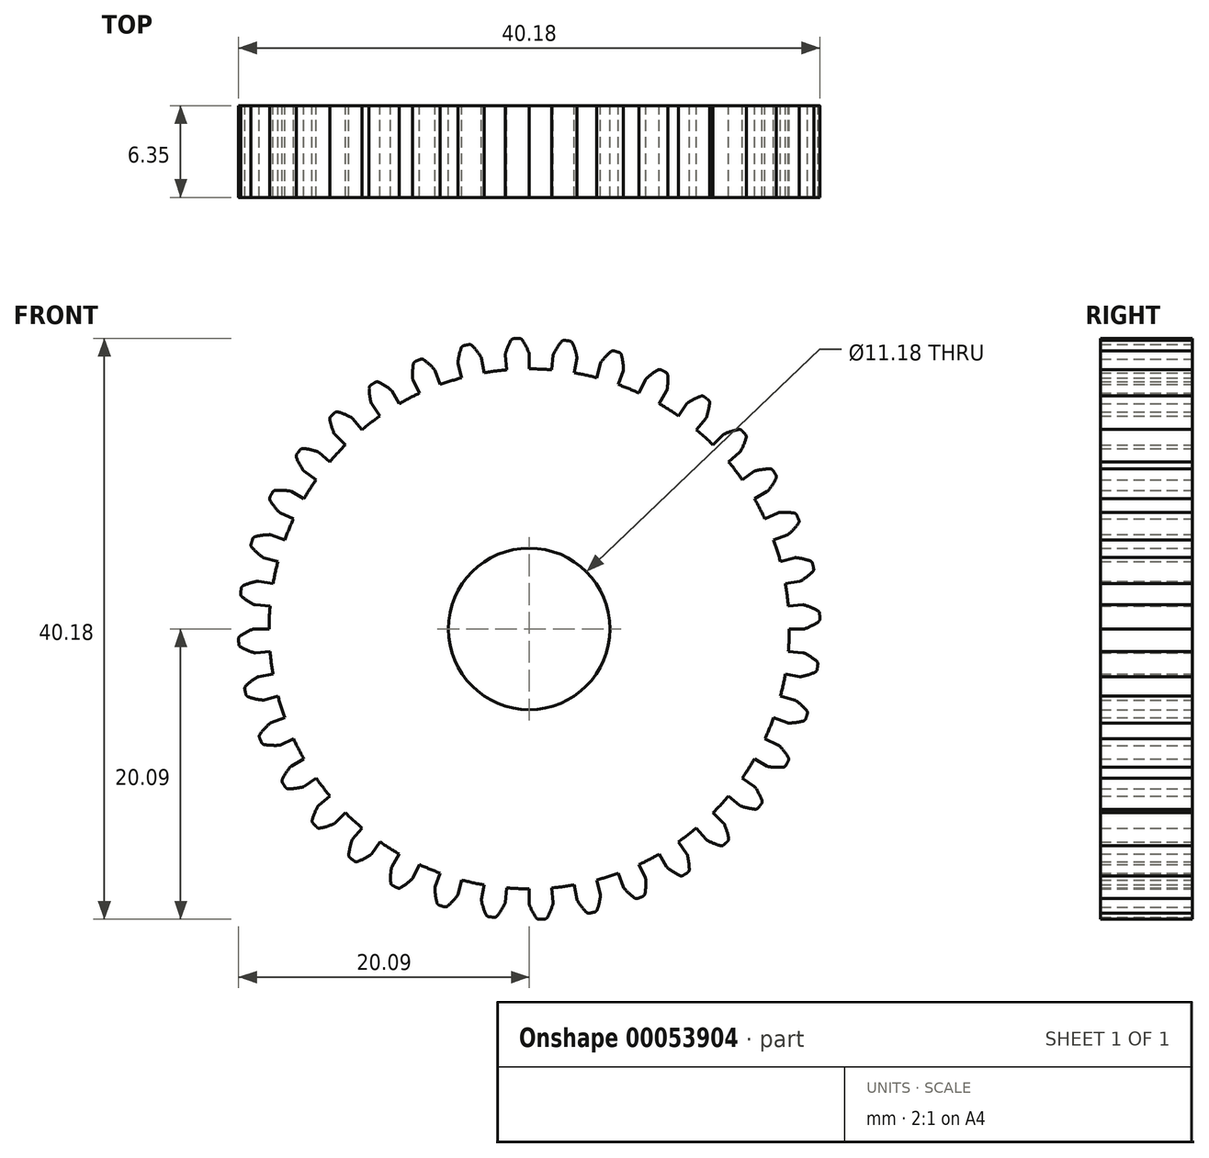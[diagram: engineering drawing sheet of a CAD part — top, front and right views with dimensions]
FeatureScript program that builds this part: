
annotation { "Feature Type Name" : "Feature", "Feature Type Description" : "" }
export const myFeature = defineFeature(function(context is Context, id is Id, definition is map)
    precondition{}
    {
        {
            var Q0;
            Q0=qCreatedBy(makeId("Front.planeOp"),FACE);
            var sketch = newSketch(context, id + "F0", { "sketchPlane" : qUnion([Q0])});
            skCircle(sketch, "E0", {"center": v(0, 0) * mm, "radius": 17.98 * mm});
            skArc(sketch, "E1", {"start": v(-0.7, 20.1) * mm, "mid": v(-0.79, 20.09) * mm, "end": v(-0.88, 20.08) * mm});
            skArc(sketch, "E2.trimOffspring", {"start": v(-0.02, 19.1) * mm, "mid": v(-0.23, 19.55) * mm, "end": v(-0.48, 19.98) * mm});
            skLineSegment(sketch, "E3", {"start": v(0, 19) * mm, "end": v(0, 17.98) * mm});
            skArc(sketch, "E4.MirrorCS", {"start": v(-1.05, 20.08) * mm, "mid": v(-0.97, 20.08) * mm, "end": v(-0.88, 20.08) * mm});
            skArc(sketch, "E5.MirrorCS", {"start": v(-1.65, 19.02) * mm, "mid": v(-1.48, 19.5) * mm, "end": v(-1.26, 19.94) * mm});
            skLineSegment(sketch, "E6.MirrorCS", {"start": v(-1.66, 18.93) * mm, "end": v(-1.57, 17.91) * mm});
            skPoint(sketch, "E7.visualSharp", {"position": v(-1.66, 18.98) * mm});
            skArc(sketch, "E7.filletArc", {"start": v(-1.65, 19.02) * mm, "mid": v(-1.66, 18.98) * mm, "end": v(-1.66, 18.93) * mm});
            skPoint(sketch, "E8.visualSharp", {"position": v(-1.2, 20.07) * mm});
            skArc(sketch, "E8.filletArc", {"start": v(-1.05, 20.08) * mm, "mid": v(-1.18, 20.04) * mm, "end": v(-1.26, 19.94) * mm});
            skPoint(sketch, "E9.visualSharp", {"position": v(-0.56, 20.1) * mm});
            skArc(sketch, "E9.filletArc", {"start": v(-0.48, 19.98) * mm, "mid": v(-0.58, 20.06) * mm, "end": v(-0.7, 20.1) * mm});
            skPoint(sketch, "E10.visualSharp", {"position": v(0, 19.05) * mm});
            skArc(sketch, "E10.filletArc", {"start": v(0, 19) * mm, "mid": v(0, 19.05) * mm, "end": v(-0.02, 19.1) * mm});
            skLineSegment(sketch, "E11.1.0", {"start": v(-3.3, 18.71) * mm, "end": v(-3.12, 17.7) * mm});
            skPoint(sketch, "E11.1.1", {"position": v(-4.93, 18.4) * mm});
            skArc(sketch, "E11.1.2", {"start": v(-3.33, 18.8) * mm, "mid": v(-3.62, 19.21) * mm, "end": v(-3.94, 19.6) * mm});
            skPoint(sketch, "E11.1.3", {"position": v(-3.3, 18.76) * mm});
            skArc(sketch, "E11.1.4", {"start": v(-4.93, 18.45) * mm, "mid": v(-4.84, 18.94) * mm, "end": v(-4.7, 19.42) * mm});
            skPoint(sketch, "E11.1.5", {"position": v(-4.66, 19.56) * mm});
            skPoint(sketch, "E11.1.6", {"position": v(-4.04, 19.7) * mm});
            skLineSegment(sketch, "E11.1.7", {"start": v(-4.92, 18.35) * mm, "end": v(-4.65, 17.37) * mm});
            skArc(sketch, "E11.1.8", {"start": v(-4.52, 19.59) * mm, "mid": v(-4.64, 19.53) * mm, "end": v(-4.7, 19.42) * mm});
            skArc(sketch, "E11.1.9", {"start": v(-4.52, 19.59) * mm, "mid": v(-4.44, 19.6) * mm, "end": v(-4.35, 19.63) * mm});
            skArc(sketch, "E11.1.10", {"start": v(-3.94, 19.6) * mm, "mid": v(-4.05, 19.66) * mm, "end": v(-4.18, 19.67) * mm});
            skArc(sketch, "E11.1.11", {"start": v(-4.18, 19.67) * mm, "mid": v(-4.27, 19.65) * mm, "end": v(-4.35, 19.63) * mm});
            skArc(sketch, "E11.1.12", {"start": v(-4.93, 18.45) * mm, "mid": v(-4.93, 18.4) * mm, "end": v(-4.92, 18.35) * mm});
            skArc(sketch, "E11.1.13", {"start": v(-3.3, 18.71) * mm, "mid": v(-3.31, 18.76) * mm, "end": v(-3.33, 18.8) * mm});
            skLineSegment(sketch, "E11.2.0", {"start": v(-6.5, 17.86) * mm, "end": v(-6.15, 16.9) * mm});
            skPoint(sketch, "E11.2.1", {"position": v(-8.05, 17.27) * mm});
            skArc(sketch, "E11.2.2", {"start": v(-6.55, 17.94) * mm, "mid": v(-6.9, 18.3) * mm, "end": v(-7.28, 18.6) * mm});
            skPoint(sketch, "E11.2.3", {"position": v(-6.52, 17.9) * mm});
            skArc(sketch, "E11.2.4", {"start": v(-8.05, 17.31) * mm, "mid": v(-8.06, 17.81) * mm, "end": v(-8, 18.3) * mm});
            skPoint(sketch, "E11.2.5", {"position": v(-7.98, 18.45) * mm});
            skPoint(sketch, "E11.2.6", {"position": v(-7.4, 18.7) * mm});
            skLineSegment(sketch, "E11.2.7", {"start": v(-8.03, 17.22) * mm, "end": v(-7.6, 16.3) * mm});
            skArc(sketch, "E11.2.8", {"start": v(-7.86, 18.5) * mm, "mid": v(-7.96, 18.43) * mm, "end": v(-8, 18.3) * mm});
            skArc(sketch, "E11.2.9", {"start": v(-7.86, 18.5) * mm, "mid": v(-7.78, 18.54) * mm, "end": v(-7.7, 18.57) * mm});
            skArc(sketch, "E11.2.10", {"start": v(-7.28, 18.6) * mm, "mid": v(-7.4, 18.66) * mm, "end": v(-7.53, 18.64) * mm});
            skArc(sketch, "E11.2.11", {"start": v(-7.53, 18.64) * mm, "mid": v(-7.61, 18.6) * mm, "end": v(-7.7, 18.57) * mm});
            skArc(sketch, "E11.2.12", {"start": v(-8.05, 17.31) * mm, "mid": v(-8.05, 17.27) * mm, "end": v(-8.03, 17.22) * mm});
            skArc(sketch, "E11.2.13", {"start": v(-6.5, 17.86) * mm, "mid": v(-6.52, 17.9) * mm, "end": v(-6.55, 17.94) * mm});
            skLineSegment(sketch, "E11.3.0", {"start": v(-9.5, 16.46) * mm, "end": v(-9, 15.57) * mm});
            skPoint(sketch, "E11.3.1", {"position": v(-10.93, 15.6) * mm});
            skArc(sketch, "E11.3.2", {"start": v(-9.56, 16.53) * mm, "mid": v(-9.97, 16.82) * mm, "end": v(-10.4, 17.06) * mm});
            skPoint(sketch, "E11.3.3", {"position": v(-9.52, 16.5) * mm});
            skArc(sketch, "E11.3.4", {"start": v(-10.94, 15.65) * mm, "mid": v(-11.03, 16.14) * mm, "end": v(-11.07, 16.64) * mm});
            skPoint(sketch, "E11.3.5", {"position": v(-11.07, 16.78) * mm});
            skPoint(sketch, "E11.3.6", {"position": v(-10.53, 17.12) * mm});
            skLineSegment(sketch, "E11.3.7", {"start": v(-10.9, 15.57) * mm, "end": v(-10.31, 14.73) * mm});
            skArc(sketch, "E11.3.8", {"start": v(-10.95, 16.86) * mm, "mid": v(-11.04, 16.77) * mm, "end": v(-11.07, 16.64) * mm});
            skArc(sketch, "E11.3.9", {"start": v(-10.95, 16.86) * mm, "mid": v(-10.88, 16.9) * mm, "end": v(-10.8, 16.96) * mm});
            skArc(sketch, "E11.3.10", {"start": v(-10.4, 17.06) * mm, "mid": v(-10.53, 17.09) * mm, "end": v(-10.65, 17.05) * mm});
            skArc(sketch, "E11.3.11", {"start": v(-10.65, 17.05) * mm, "mid": v(-10.73, 17) * mm, "end": v(-10.8, 16.96) * mm});
            skArc(sketch, "E11.3.12", {"start": v(-10.94, 15.65) * mm, "mid": v(-10.92, 15.6) * mm, "end": v(-10.9, 15.57) * mm});
            skArc(sketch, "E11.3.13", {"start": v(-9.5, 16.46) * mm, "mid": v(-9.53, 16.5) * mm, "end": v(-9.56, 16.53) * mm});
            skLineSegment(sketch, "E11.4.0", {"start": v(-12.21, 14.56) * mm, "end": v(-11.56, 13.78) * mm});
            skPoint(sketch, "E11.4.1", {"position": v(-13.47, 13.47) * mm});
            skArc(sketch, "E11.4.2", {"start": v(-12.29, 14.62) * mm, "mid": v(-12.74, 14.83) * mm, "end": v(-13.2, 15) * mm});
            skPoint(sketch, "E11.4.3", {"position": v(-12.25, 14.6) * mm});
            skArc(sketch, "E11.4.4", {"start": v(-13.5, 13.52) * mm, "mid": v(-13.66, 13.98) * mm, "end": v(-13.79, 14.47) * mm});
            skPoint(sketch, "E11.4.5", {"position": v(-13.81, 14.6) * mm});
            skPoint(sketch, "E11.4.6", {"position": v(-13.35, 15.03) * mm});
            skLineSegment(sketch, "E11.4.7", {"start": v(-13.44, 13.44) * mm, "end": v(-12.72, 12.72) * mm});
            skArc(sketch, "E11.4.8", {"start": v(-13.71, 14.7) * mm, "mid": v(-13.78, 14.6) * mm, "end": v(-13.79, 14.47) * mm});
            skArc(sketch, "E11.4.9", {"start": v(-13.71, 14.7) * mm, "mid": v(-13.65, 14.76) * mm, "end": v(-13.58, 14.82) * mm});
            skArc(sketch, "E11.4.10", {"start": v(-13.2, 15) * mm, "mid": v(-13.34, 15) * mm, "end": v(-13.45, 14.94) * mm});
            skArc(sketch, "E11.4.11", {"start": v(-13.45, 14.94) * mm, "mid": v(-13.52, 14.88) * mm, "end": v(-13.58, 14.82) * mm});
            skArc(sketch, "E11.4.12", {"start": v(-13.5, 13.52) * mm, "mid": v(-13.47, 13.47) * mm, "end": v(-13.44, 13.44) * mm});
            skArc(sketch, "E11.4.13", {"start": v(-12.21, 14.56) * mm, "mid": v(-12.25, 14.6) * mm, "end": v(-12.29, 14.62) * mm});
            skLineSegment(sketch, "E11.5.0", {"start": v(-14.56, 12.21) * mm, "end": v(-13.78, 11.56) * mm});
            skPoint(sketch, "E11.5.1", {"position": v(-15.6, 10.93) * mm});
            skArc(sketch, "E11.5.2", {"start": v(-14.64, 12.26) * mm, "mid": v(-15.12, 12.4) * mm, "end": v(-15.61, 12.47) * mm});
            skPoint(sketch, "E11.5.3", {"position": v(-14.6, 12.25) * mm});
            skArc(sketch, "E11.5.4", {"start": v(-15.63, 10.97) * mm, "mid": v(-15.88, 11.4) * mm, "end": v(-16.1, 11.85) * mm});
            skPoint(sketch, "E11.5.5", {"position": v(-16.14, 11.99) * mm});
            skPoint(sketch, "E11.5.6", {"position": v(-15.76, 12.49) * mm});
            skLineSegment(sketch, "E11.5.7", {"start": v(-15.57, 10.9) * mm, "end": v(-14.73, 10.31) * mm});
            skArc(sketch, "E11.5.8", {"start": v(-16.06, 12.1) * mm, "mid": v(-16.1, 11.98) * mm, "end": v(-16.1, 11.85) * mm});
            skArc(sketch, "E11.5.9", {"start": v(-16.06, 12.1) * mm, "mid": v(-16, 12.17) * mm, "end": v(-15.95, 12.24) * mm});
            skArc(sketch, "E11.5.10", {"start": v(-15.61, 12.47) * mm, "mid": v(-15.74, 12.46) * mm, "end": v(-15.84, 12.38) * mm});
            skArc(sketch, "E11.5.11", {"start": v(-15.84, 12.38) * mm, "mid": v(-15.9, 12.3) * mm, "end": v(-15.95, 12.24) * mm});
            skArc(sketch, "E11.5.12", {"start": v(-15.63, 10.97) * mm, "mid": v(-15.6, 10.93) * mm, "end": v(-15.57, 10.9) * mm});
            skArc(sketch, "E11.5.13", {"start": v(-14.56, 12.21) * mm, "mid": v(-14.6, 12.24) * mm, "end": v(-14.64, 12.26) * mm});
            skLineSegment(sketch, "E11.6.0", {"start": v(-16.46, 9.5) * mm, "end": v(-15.57, 9) * mm});
            skPoint(sketch, "E11.6.1", {"position": v(-17.27, 8.05) * mm});
            skArc(sketch, "E11.6.2", {"start": v(-16.55, 9.53) * mm, "mid": v(-17.04, 9.58) * mm, "end": v(-17.54, 9.57) * mm});
            skPoint(sketch, "E11.6.3", {"position": v(-16.5, 9.53) * mm});
            skArc(sketch, "E11.6.4", {"start": v(-17.3, 8.09) * mm, "mid": v(-17.62, 8.47) * mm, "end": v(-17.9, 8.88) * mm});
            skPoint(sketch, "E11.6.5", {"position": v(-17.98, 9) * mm});
            skPoint(sketch, "E11.6.6", {"position": v(-17.68, 9.56) * mm});
            skLineSegment(sketch, "E11.6.7", {"start": v(-17.22, 8.03) * mm, "end": v(-16.3, 7.6) * mm});
            skArc(sketch, "E11.6.8", {"start": v(-17.91, 9.13) * mm, "mid": v(-17.94, 9) * mm, "end": v(-17.9, 8.88) * mm});
            skArc(sketch, "E11.6.9", {"start": v(-17.91, 9.13) * mm, "mid": v(-17.87, 9.2) * mm, "end": v(-17.83, 9.28) * mm});
            skArc(sketch, "E11.6.10", {"start": v(-17.54, 9.57) * mm, "mid": v(-17.66, 9.53) * mm, "end": v(-17.75, 9.44) * mm});
            skArc(sketch, "E11.6.11", {"start": v(-17.75, 9.44) * mm, "mid": v(-17.8, 9.36) * mm, "end": v(-17.83, 9.28) * mm});
            skArc(sketch, "E11.6.12", {"start": v(-17.3, 8.09) * mm, "mid": v(-17.26, 8.05) * mm, "end": v(-17.22, 8.03) * mm});
            skArc(sketch, "E11.6.13", {"start": v(-16.46, 9.5) * mm, "mid": v(-16.5, 9.52) * mm, "end": v(-16.55, 9.53) * mm});
            skLineSegment(sketch, "E11.7.0", {"start": v(-17.86, 6.5) * mm, "end": v(-16.9, 6.15) * mm});
            skPoint(sketch, "E11.7.1", {"position": v(-18.4, 4.93) * mm});
            skArc(sketch, "E11.7.2", {"start": v(-17.95, 6.51) * mm, "mid": v(-18.45, 6.47) * mm, "end": v(-18.94, 6.38) * mm});
            skPoint(sketch, "E11.7.3", {"position": v(-17.9, 6.52) * mm});
            skArc(sketch, "E11.7.4", {"start": v(-18.44, 4.96) * mm, "mid": v(-18.82, 5.28) * mm, "end": v(-19.17, 5.63) * mm});
            skPoint(sketch, "E11.7.5", {"position": v(-19.27, 5.74) * mm});
            skPoint(sketch, "E11.7.6", {"position": v(-19.08, 6.35) * mm});
            skLineSegment(sketch, "E11.7.7", {"start": v(-18.35, 4.92) * mm, "end": v(-17.37, 4.65) * mm});
            skArc(sketch, "E11.7.8", {"start": v(-19.23, 5.88) * mm, "mid": v(-19.23, 5.75) * mm, "end": v(-19.17, 5.63) * mm});
            skArc(sketch, "E11.7.9", {"start": v(-19.23, 5.88) * mm, "mid": v(-19.2, 5.96) * mm, "end": v(-19.17, 6.05) * mm});
            skArc(sketch, "E11.7.10", {"start": v(-18.94, 6.38) * mm, "mid": v(-19.05, 6.32) * mm, "end": v(-19.12, 6.21) * mm});
            skArc(sketch, "E11.7.11", {"start": v(-19.12, 6.21) * mm, "mid": v(-19.15, 6.13) * mm, "end": v(-19.17, 6.05) * mm});
            skArc(sketch, "E11.7.12", {"start": v(-18.44, 4.96) * mm, "mid": v(-18.4, 4.93) * mm, "end": v(-18.35, 4.92) * mm});
            skArc(sketch, "E11.7.13", {"start": v(-17.86, 6.5) * mm, "mid": v(-17.9, 6.51) * mm, "end": v(-17.95, 6.51) * mm});
            skLineSegment(sketch, "E11.8.0", {"start": v(-18.71, 3.3) * mm, "end": v(-17.7, 3.12) * mm});
            skPoint(sketch, "E11.8.1", {"position": v(-18.98, 1.66) * mm});
            skArc(sketch, "E11.8.2", {"start": v(-18.8, 3.3) * mm, "mid": v(-19.3, 3.17) * mm, "end": v(-19.76, 3) * mm});
            skPoint(sketch, "E11.8.3", {"position": v(-18.76, 3.3) * mm});
            skArc(sketch, "E11.8.4", {"start": v(-19.02, 1.68) * mm, "mid": v(-19.46, 1.93) * mm, "end": v(-19.86, 2.22) * mm});
            skPoint(sketch, "E11.8.5", {"position": v(-19.97, 2.31) * mm});
            skPoint(sketch, "E11.8.6", {"position": v(-19.89, 2.94) * mm});
            skLineSegment(sketch, "E11.8.7", {"start": v(-18.93, 1.66) * mm, "end": v(-17.91, 1.57) * mm});
            skArc(sketch, "E11.8.8", {"start": v(-19.95, 2.45) * mm, "mid": v(-19.94, 2.32) * mm, "end": v(-19.86, 2.22) * mm});
            skArc(sketch, "E11.8.9", {"start": v(-19.95, 2.45) * mm, "mid": v(-19.94, 2.54) * mm, "end": v(-19.93, 2.62) * mm});
            skArc(sketch, "E11.8.10", {"start": v(-19.76, 3) * mm, "mid": v(-19.86, 2.92) * mm, "end": v(-19.9, 2.8) * mm});
            skArc(sketch, "E11.8.11", {"start": v(-19.9, 2.8) * mm, "mid": v(-19.92, 2.71) * mm, "end": v(-19.93, 2.62) * mm});
            skArc(sketch, "E11.8.12", {"start": v(-19.02, 1.68) * mm, "mid": v(-18.98, 1.66) * mm, "end": v(-18.93, 1.66) * mm});
            skArc(sketch, "E11.8.13", {"start": v(-18.71, 3.3) * mm, "mid": v(-18.76, 3.3) * mm, "end": v(-18.8, 3.3) * mm});
            skLineSegment(sketch, "E11.9.0", {"start": v(-19, 0) * mm, "end": v(-17.98, 0) * mm});
            skPoint(sketch, "E11.9.1", {"position": v(-18.98, -1.66) * mm});
            skArc(sketch, "E11.9.2", {"start": v(-19.1, -0.02) * mm, "mid": v(-19.55, -0.23) * mm, "end": v(-19.98, -0.48) * mm});
            skPoint(sketch, "E11.9.3", {"position": v(-19.05, 0) * mm});
            skArc(sketch, "E11.9.4", {"start": v(-19.02, -1.65) * mm, "mid": v(-19.5, -1.48) * mm, "end": v(-19.94, -1.26) * mm});
            skPoint(sketch, "E11.9.5", {"position": v(-20.07, -1.2) * mm});
            skPoint(sketch, "E11.9.6", {"position": v(-20.1, -0.56) * mm});
            skLineSegment(sketch, "E11.9.7", {"start": v(-18.93, -1.66) * mm, "end": v(-17.91, -1.57) * mm});
            skArc(sketch, "E11.9.8", {"start": v(-20.08, -1.05) * mm, "mid": v(-20.04, -1.18) * mm, "end": v(-19.94, -1.26) * mm});
            skArc(sketch, "E11.9.9", {"start": v(-20.08, -1.05) * mm, "mid": v(-20.08, -0.97) * mm, "end": v(-20.08, -0.88) * mm});
            skArc(sketch, "E11.9.10", {"start": v(-19.98, -0.48) * mm, "mid": v(-20.06, -0.58) * mm, "end": v(-20.1, -0.7) * mm});
            skArc(sketch, "E11.9.11", {"start": v(-20.1, -0.7) * mm, "mid": v(-20.09, -0.79) * mm, "end": v(-20.08, -0.88) * mm});
            skArc(sketch, "E11.9.12", {"start": v(-19.02, -1.65) * mm, "mid": v(-18.98, -1.66) * mm, "end": v(-18.93, -1.66) * mm});
            skArc(sketch, "E11.9.13", {"start": v(-19, 0) * mm, "mid": v(-19.05, 0) * mm, "end": v(-19.1, -0.02) * mm});
            skLineSegment(sketch, "E11.10.0", {"start": v(-18.71, -3.3) * mm, "end": v(-17.7, -3.12) * mm});
            skPoint(sketch, "E11.10.1", {"position": v(-18.4, -4.93) * mm});
            skArc(sketch, "E11.10.2", {"start": v(-18.8, -3.33) * mm, "mid": v(-19.21, -3.62) * mm, "end": v(-19.6, -3.94) * mm});
            skPoint(sketch, "E11.10.3", {"position": v(-18.76, -3.3) * mm});
            skArc(sketch, "E11.10.4", {"start": v(-18.45, -4.93) * mm, "mid": v(-18.94, -4.84) * mm, "end": v(-19.42, -4.7) * mm});
            skPoint(sketch, "E11.10.5", {"position": v(-19.56, -4.66) * mm});
            skPoint(sketch, "E11.10.6", {"position": v(-19.7, -4.04) * mm});
            skLineSegment(sketch, "E11.10.7", {"start": v(-18.35, -4.92) * mm, "end": v(-17.37, -4.65) * mm});
            skArc(sketch, "E11.10.8", {"start": v(-19.59, -4.52) * mm, "mid": v(-19.53, -4.64) * mm, "end": v(-19.42, -4.7) * mm});
            skArc(sketch, "E11.10.9", {"start": v(-19.59, -4.52) * mm, "mid": v(-19.6, -4.44) * mm, "end": v(-19.63, -4.35) * mm});
            skArc(sketch, "E11.10.10", {"start": v(-19.6, -3.94) * mm, "mid": v(-19.66, -4.05) * mm, "end": v(-19.67, -4.18) * mm});
            skArc(sketch, "E11.10.11", {"start": v(-19.67, -4.18) * mm, "mid": v(-19.65, -4.27) * mm, "end": v(-19.63, -4.35) * mm});
            skArc(sketch, "E11.10.12", {"start": v(-18.45, -4.93) * mm, "mid": v(-18.4, -4.93) * mm, "end": v(-18.35, -4.92) * mm});
            skArc(sketch, "E11.10.13", {"start": v(-18.71, -3.3) * mm, "mid": v(-18.76, -3.31) * mm, "end": v(-18.8, -3.33) * mm});
            skLineSegment(sketch, "E11.11.0", {"start": v(-17.86, -6.5) * mm, "end": v(-16.9, -6.15) * mm});
            skPoint(sketch, "E11.11.1", {"position": v(-17.27, -8.05) * mm});
            skArc(sketch, "E11.11.2", {"start": v(-17.94, -6.55) * mm, "mid": v(-18.3, -6.9) * mm, "end": v(-18.6, -7.28) * mm});
            skPoint(sketch, "E11.11.3", {"position": v(-17.9, -6.52) * mm});
            skArc(sketch, "E11.11.4", {"start": v(-17.31, -8.05) * mm, "mid": v(-17.81, -8.06) * mm, "end": v(-18.3, -8) * mm});
            skPoint(sketch, "E11.11.5", {"position": v(-18.45, -7.98) * mm});
            skPoint(sketch, "E11.11.6", {"position": v(-18.7, -7.4) * mm});
            skLineSegment(sketch, "E11.11.7", {"start": v(-17.22, -8.03) * mm, "end": v(-16.3, -7.6) * mm});
            skArc(sketch, "E11.11.8", {"start": v(-18.5, -7.86) * mm, "mid": v(-18.43, -7.96) * mm, "end": v(-18.3, -8) * mm});
            skArc(sketch, "E11.11.9", {"start": v(-18.5, -7.86) * mm, "mid": v(-18.54, -7.78) * mm, "end": v(-18.57, -7.7) * mm});
            skArc(sketch, "E11.11.10", {"start": v(-18.6, -7.28) * mm, "mid": v(-18.66, -7.4) * mm, "end": v(-18.64, -7.53) * mm});
            skArc(sketch, "E11.11.11", {"start": v(-18.64, -7.53) * mm, "mid": v(-18.6, -7.61) * mm, "end": v(-18.57, -7.7) * mm});
            skArc(sketch, "E11.11.12", {"start": v(-17.31, -8.05) * mm, "mid": v(-17.27, -8.05) * mm, "end": v(-17.22, -8.03) * mm});
            skArc(sketch, "E11.11.13", {"start": v(-17.86, -6.5) * mm, "mid": v(-17.9, -6.52) * mm, "end": v(-17.94, -6.55) * mm});
            skLineSegment(sketch, "E11.12.0", {"start": v(-16.46, -9.5) * mm, "end": v(-15.57, -9) * mm});
            skPoint(sketch, "E11.12.1", {"position": v(-15.6, -10.93) * mm});
            skArc(sketch, "E11.12.2", {"start": v(-16.53, -9.56) * mm, "mid": v(-16.82, -9.97) * mm, "end": v(-17.06, -10.4) * mm});
            skPoint(sketch, "E11.12.3", {"position": v(-16.5, -9.52) * mm});
            skArc(sketch, "E11.12.4", {"start": v(-15.65, -10.94) * mm, "mid": v(-16.14, -11.03) * mm, "end": v(-16.64, -11.07) * mm});
            skPoint(sketch, "E11.12.5", {"position": v(-16.78, -11.07) * mm});
            skPoint(sketch, "E11.12.6", {"position": v(-17.12, -10.53) * mm});
            skLineSegment(sketch, "E11.12.7", {"start": v(-15.57, -10.9) * mm, "end": v(-14.73, -10.31) * mm});
            skArc(sketch, "E11.12.8", {"start": v(-16.86, -10.95) * mm, "mid": v(-16.77, -11.04) * mm, "end": v(-16.64, -11.07) * mm});
            skArc(sketch, "E11.12.9", {"start": v(-16.86, -10.95) * mm, "mid": v(-16.9, -10.88) * mm, "end": v(-16.96, -10.8) * mm});
            skArc(sketch, "E11.12.10", {"start": v(-17.06, -10.4) * mm, "mid": v(-17.09, -10.53) * mm, "end": v(-17.05, -10.65) * mm});
            skArc(sketch, "E11.12.11", {"start": v(-17.05, -10.65) * mm, "mid": v(-17, -10.73) * mm, "end": v(-16.96, -10.8) * mm});
            skArc(sketch, "E11.12.12", {"start": v(-15.65, -10.94) * mm, "mid": v(-15.6, -10.92) * mm, "end": v(-15.57, -10.9) * mm});
            skArc(sketch, "E11.12.13", {"start": v(-16.46, -9.5) * mm, "mid": v(-16.5, -9.53) * mm, "end": v(-16.53, -9.56) * mm});
            skLineSegment(sketch, "E11.13.0", {"start": v(-14.56, -12.21) * mm, "end": v(-13.78, -11.56) * mm});
            skPoint(sketch, "E11.13.1", {"position": v(-13.47, -13.47) * mm});
            skArc(sketch, "E11.13.2", {"start": v(-14.62, -12.29) * mm, "mid": v(-14.83, -12.74) * mm, "end": v(-15, -13.2) * mm});
            skPoint(sketch, "E11.13.3", {"position": v(-14.6, -12.25) * mm});
            skArc(sketch, "E11.13.4", {"start": v(-13.52, -13.5) * mm, "mid": v(-13.98, -13.66) * mm, "end": v(-14.47, -13.79) * mm});
            skPoint(sketch, "E11.13.5", {"position": v(-14.6, -13.81) * mm});
            skPoint(sketch, "E11.13.6", {"position": v(-15.03, -13.35) * mm});
            skLineSegment(sketch, "E11.13.7", {"start": v(-13.44, -13.44) * mm, "end": v(-12.72, -12.72) * mm});
            skArc(sketch, "E11.13.8", {"start": v(-14.7, -13.71) * mm, "mid": v(-14.6, -13.78) * mm, "end": v(-14.47, -13.79) * mm});
            skArc(sketch, "E11.13.9", {"start": v(-14.7, -13.71) * mm, "mid": v(-14.76, -13.65) * mm, "end": v(-14.82, -13.58) * mm});
            skArc(sketch, "E11.13.10", {"start": v(-15, -13.2) * mm, "mid": v(-15, -13.34) * mm, "end": v(-14.94, -13.45) * mm});
            skArc(sketch, "E11.13.11", {"start": v(-14.94, -13.45) * mm, "mid": v(-14.88, -13.52) * mm, "end": v(-14.82, -13.58) * mm});
            skArc(sketch, "E11.13.12", {"start": v(-13.52, -13.5) * mm, "mid": v(-13.47, -13.47) * mm, "end": v(-13.44, -13.44) * mm});
            skArc(sketch, "E11.13.13", {"start": v(-14.56, -12.21) * mm, "mid": v(-14.6, -12.25) * mm, "end": v(-14.62, -12.29) * mm});
            skLineSegment(sketch, "E11.14.0", {"start": v(-12.21, -14.56) * mm, "end": v(-11.56, -13.78) * mm});
            skPoint(sketch, "E11.14.1", {"position": v(-10.93, -15.6) * mm});
            skArc(sketch, "E11.14.2", {"start": v(-12.26, -14.64) * mm, "mid": v(-12.4, -15.12) * mm, "end": v(-12.47, -15.61) * mm});
            skPoint(sketch, "E11.14.3", {"position": v(-12.25, -14.6) * mm});
            skArc(sketch, "E11.14.4", {"start": v(-10.97, -15.63) * mm, "mid": v(-11.4, -15.88) * mm, "end": v(-11.85, -16.1) * mm});
            skPoint(sketch, "E11.14.5", {"position": v(-11.99, -16.14) * mm});
            skPoint(sketch, "E11.14.6", {"position": v(-12.49, -15.76) * mm});
            skLineSegment(sketch, "E11.14.7", {"start": v(-10.9, -15.57) * mm, "end": v(-10.31, -14.73) * mm});
            skArc(sketch, "E11.14.8", {"start": v(-12.1, -16.06) * mm, "mid": v(-11.98, -16.1) * mm, "end": v(-11.85, -16.1) * mm});
            skArc(sketch, "E11.14.9", {"start": v(-12.1, -16.06) * mm, "mid": v(-12.17, -16) * mm, "end": v(-12.24, -15.95) * mm});
            skArc(sketch, "E11.14.10", {"start": v(-12.47, -15.61) * mm, "mid": v(-12.46, -15.74) * mm, "end": v(-12.38, -15.84) * mm});
            skArc(sketch, "E11.14.11", {"start": v(-12.38, -15.84) * mm, "mid": v(-12.3, -15.9) * mm, "end": v(-12.24, -15.95) * mm});
            skArc(sketch, "E11.14.12", {"start": v(-10.97, -15.63) * mm, "mid": v(-10.93, -15.6) * mm, "end": v(-10.9, -15.57) * mm});
            skArc(sketch, "E11.14.13", {"start": v(-12.21, -14.56) * mm, "mid": v(-12.24, -14.6) * mm, "end": v(-12.26, -14.64) * mm});
            skLineSegment(sketch, "E11.15.0", {"start": v(-9.5, -16.46) * mm, "end": v(-9, -15.57) * mm});
            skPoint(sketch, "E11.15.1", {"position": v(-8.05, -17.27) * mm});
            skArc(sketch, "E11.15.2", {"start": v(-9.53, -16.55) * mm, "mid": v(-9.58, -17.04) * mm, "end": v(-9.57, -17.54) * mm});
            skPoint(sketch, "E11.15.3", {"position": v(-9.53, -16.5) * mm});
            skArc(sketch, "E11.15.4", {"start": v(-8.09, -17.3) * mm, "mid": v(-8.47, -17.62) * mm, "end": v(-8.88, -17.9) * mm});
            skPoint(sketch, "E11.15.5", {"position": v(-9, -17.98) * mm});
            skPoint(sketch, "E11.15.6", {"position": v(-9.56, -17.68) * mm});
            skLineSegment(sketch, "E11.15.7", {"start": v(-8.03, -17.22) * mm, "end": v(-7.6, -16.3) * mm});
            skArc(sketch, "E11.15.8", {"start": v(-9.13, -17.91) * mm, "mid": v(-9, -17.94) * mm, "end": v(-8.88, -17.9) * mm});
            skArc(sketch, "E11.15.9", {"start": v(-9.13, -17.91) * mm, "mid": v(-9.2, -17.87) * mm, "end": v(-9.28, -17.83) * mm});
            skArc(sketch, "E11.15.10", {"start": v(-9.57, -17.54) * mm, "mid": v(-9.53, -17.66) * mm, "end": v(-9.44, -17.75) * mm});
            skArc(sketch, "E11.15.11", {"start": v(-9.44, -17.75) * mm, "mid": v(-9.36, -17.8) * mm, "end": v(-9.28, -17.83) * mm});
            skArc(sketch, "E11.15.12", {"start": v(-8.09, -17.3) * mm, "mid": v(-8.05, -17.26) * mm, "end": v(-8.03, -17.22) * mm});
            skArc(sketch, "E11.15.13", {"start": v(-9.5, -16.46) * mm, "mid": v(-9.52, -16.5) * mm, "end": v(-9.53, -16.55) * mm});
            skLineSegment(sketch, "E11.16.0", {"start": v(-6.5, -17.86) * mm, "end": v(-6.15, -16.9) * mm});
            skPoint(sketch, "E11.16.1", {"position": v(-4.93, -18.4) * mm});
            skArc(sketch, "E11.16.2", {"start": v(-6.51, -17.95) * mm, "mid": v(-6.47, -18.45) * mm, "end": v(-6.38, -18.94) * mm});
            skPoint(sketch, "E11.16.3", {"position": v(-6.52, -17.9) * mm});
            skArc(sketch, "E11.16.4", {"start": v(-4.96, -18.44) * mm, "mid": v(-5.28, -18.82) * mm, "end": v(-5.63, -19.17) * mm});
            skPoint(sketch, "E11.16.5", {"position": v(-5.74, -19.27) * mm});
            skPoint(sketch, "E11.16.6", {"position": v(-6.35, -19.08) * mm});
            skLineSegment(sketch, "E11.16.7", {"start": v(-4.92, -18.35) * mm, "end": v(-4.65, -17.37) * mm});
            skArc(sketch, "E11.16.8", {"start": v(-5.88, -19.23) * mm, "mid": v(-5.75, -19.23) * mm, "end": v(-5.63, -19.17) * mm});
            skArc(sketch, "E11.16.9", {"start": v(-5.88, -19.23) * mm, "mid": v(-5.96, -19.2) * mm, "end": v(-6.05, -19.17) * mm});
            skArc(sketch, "E11.16.10", {"start": v(-6.38, -18.94) * mm, "mid": v(-6.32, -19.05) * mm, "end": v(-6.21, -19.12) * mm});
            skArc(sketch, "E11.16.11", {"start": v(-6.21, -19.12) * mm, "mid": v(-6.13, -19.15) * mm, "end": v(-6.05, -19.17) * mm});
            skArc(sketch, "E11.16.12", {"start": v(-4.96, -18.44) * mm, "mid": v(-4.93, -18.4) * mm, "end": v(-4.92, -18.35) * mm});
            skArc(sketch, "E11.16.13", {"start": v(-6.5, -17.86) * mm, "mid": v(-6.51, -17.9) * mm, "end": v(-6.51, -17.95) * mm});
            skLineSegment(sketch, "E11.17.0", {"start": v(-3.3, -18.71) * mm, "end": v(-3.12, -17.7) * mm});
            skPoint(sketch, "E11.17.1", {"position": v(-1.66, -18.98) * mm});
            skArc(sketch, "E11.17.2", {"start": v(-3.3, -18.8) * mm, "mid": v(-3.17, -19.3) * mm, "end": v(-3, -19.76) * mm});
            skPoint(sketch, "E11.17.3", {"position": v(-3.3, -18.76) * mm});
            skArc(sketch, "E11.17.4", {"start": v(-1.68, -19.02) * mm, "mid": v(-1.93, -19.46) * mm, "end": v(-2.22, -19.86) * mm});
            skPoint(sketch, "E11.17.5", {"position": v(-2.31, -19.97) * mm});
            skPoint(sketch, "E11.17.6", {"position": v(-2.94, -19.89) * mm});
            skLineSegment(sketch, "E11.17.7", {"start": v(-1.66, -18.93) * mm, "end": v(-1.57, -17.91) * mm});
            skArc(sketch, "E11.17.8", {"start": v(-2.45, -19.95) * mm, "mid": v(-2.32, -19.94) * mm, "end": v(-2.22, -19.86) * mm});
            skArc(sketch, "E11.17.9", {"start": v(-2.45, -19.95) * mm, "mid": v(-2.54, -19.94) * mm, "end": v(-2.62, -19.93) * mm});
            skArc(sketch, "E11.17.10", {"start": v(-3, -19.76) * mm, "mid": v(-2.92, -19.86) * mm, "end": v(-2.8, -19.9) * mm});
            skArc(sketch, "E11.17.11", {"start": v(-2.8, -19.9) * mm, "mid": v(-2.71, -19.92) * mm, "end": v(-2.62, -19.93) * mm});
            skArc(sketch, "E11.17.12", {"start": v(-1.68, -19.02) * mm, "mid": v(-1.66, -18.98) * mm, "end": v(-1.66, -18.93) * mm});
            skArc(sketch, "E11.17.13", {"start": v(-3.3, -18.71) * mm, "mid": v(-3.3, -18.76) * mm, "end": v(-3.3, -18.8) * mm});
            skLineSegment(sketch, "E11.18.0", {"start": v(0, -19) * mm, "end": v(0, -17.98) * mm});
            skPoint(sketch, "E11.18.1", {"position": v(1.66, -18.98) * mm});
            skArc(sketch, "E11.18.2", {"start": v(0.02, -19.1) * mm, "mid": v(0.23, -19.55) * mm, "end": v(0.48, -19.98) * mm});
            skPoint(sketch, "E11.18.3", {"position": v(0, -19.05) * mm});
            skArc(sketch, "E11.18.4", {"start": v(1.65, -19.02) * mm, "mid": v(1.48, -19.5) * mm, "end": v(1.26, -19.94) * mm});
            skPoint(sketch, "E11.18.5", {"position": v(1.2, -20.07) * mm});
            skPoint(sketch, "E11.18.6", {"position": v(0.56, -20.1) * mm});
            skLineSegment(sketch, "E11.18.7", {"start": v(1.66, -18.93) * mm, "end": v(1.57, -17.91) * mm});
            skArc(sketch, "E11.18.8", {"start": v(1.05, -20.08) * mm, "mid": v(1.18, -20.04) * mm, "end": v(1.26, -19.94) * mm});
            skArc(sketch, "E11.18.9", {"start": v(1.05, -20.08) * mm, "mid": v(0.97, -20.08) * mm, "end": v(0.88, -20.08) * mm});
            skArc(sketch, "E11.18.10", {"start": v(0.48, -19.98) * mm, "mid": v(0.58, -20.06) * mm, "end": v(0.7, -20.1) * mm});
            skArc(sketch, "E11.18.11", {"start": v(0.7, -20.1) * mm, "mid": v(0.79, -20.09) * mm, "end": v(0.88, -20.08) * mm});
            skArc(sketch, "E11.18.12", {"start": v(1.65, -19.02) * mm, "mid": v(1.66, -18.98) * mm, "end": v(1.66, -18.93) * mm});
            skArc(sketch, "E11.18.13", {"start": v(0, -19) * mm, "mid": v(0, -19.05) * mm, "end": v(0.02, -19.1) * mm});
            skLineSegment(sketch, "E11.19.0", {"start": v(3.3, -18.71) * mm, "end": v(3.12, -17.7) * mm});
            skPoint(sketch, "E11.19.1", {"position": v(4.93, -18.4) * mm});
            skArc(sketch, "E11.19.2", {"start": v(3.33, -18.8) * mm, "mid": v(3.62, -19.21) * mm, "end": v(3.94, -19.6) * mm});
            skPoint(sketch, "E11.19.3", {"position": v(3.3, -18.76) * mm});
            skArc(sketch, "E11.19.4", {"start": v(4.93, -18.45) * mm, "mid": v(4.84, -18.94) * mm, "end": v(4.7, -19.42) * mm});
            skPoint(sketch, "E11.19.5", {"position": v(4.66, -19.56) * mm});
            skPoint(sketch, "E11.19.6", {"position": v(4.04, -19.7) * mm});
            skLineSegment(sketch, "E11.19.7", {"start": v(4.92, -18.35) * mm, "end": v(4.65, -17.37) * mm});
            skArc(sketch, "E11.19.8", {"start": v(4.52, -19.59) * mm, "mid": v(4.64, -19.53) * mm, "end": v(4.7, -19.42) * mm});
            skArc(sketch, "E11.19.9", {"start": v(4.52, -19.59) * mm, "mid": v(4.44, -19.6) * mm, "end": v(4.35, -19.63) * mm});
            skArc(sketch, "E11.19.10", {"start": v(3.94, -19.6) * mm, "mid": v(4.05, -19.66) * mm, "end": v(4.18, -19.67) * mm});
            skArc(sketch, "E11.19.11", {"start": v(4.18, -19.67) * mm, "mid": v(4.27, -19.65) * mm, "end": v(4.35, -19.63) * mm});
            skArc(sketch, "E11.19.12", {"start": v(4.93, -18.45) * mm, "mid": v(4.93, -18.4) * mm, "end": v(4.92, -18.35) * mm});
            skArc(sketch, "E11.19.13", {"start": v(3.3, -18.71) * mm, "mid": v(3.31, -18.76) * mm, "end": v(3.33, -18.8) * mm});
            skLineSegment(sketch, "E11.20.0", {"start": v(6.5, -17.86) * mm, "end": v(6.15, -16.9) * mm});
            skPoint(sketch, "E11.20.1", {"position": v(8.05, -17.27) * mm});
            skArc(sketch, "E11.20.2", {"start": v(6.55, -17.94) * mm, "mid": v(6.9, -18.3) * mm, "end": v(7.28, -18.6) * mm});
            skPoint(sketch, "E11.20.3", {"position": v(6.52, -17.9) * mm});
            skArc(sketch, "E11.20.4", {"start": v(8.05, -17.31) * mm, "mid": v(8.06, -17.81) * mm, "end": v(8, -18.3) * mm});
            skPoint(sketch, "E11.20.5", {"position": v(7.98, -18.45) * mm});
            skPoint(sketch, "E11.20.6", {"position": v(7.4, -18.7) * mm});
            skLineSegment(sketch, "E11.20.7", {"start": v(8.03, -17.22) * mm, "end": v(7.6, -16.3) * mm});
            skArc(sketch, "E11.20.8", {"start": v(7.86, -18.5) * mm, "mid": v(7.96, -18.43) * mm, "end": v(8, -18.3) * mm});
            skArc(sketch, "E11.20.9", {"start": v(7.86, -18.5) * mm, "mid": v(7.78, -18.54) * mm, "end": v(7.7, -18.57) * mm});
            skArc(sketch, "E11.20.10", {"start": v(7.28, -18.6) * mm, "mid": v(7.4, -18.66) * mm, "end": v(7.53, -18.64) * mm});
            skArc(sketch, "E11.20.11", {"start": v(7.53, -18.64) * mm, "mid": v(7.61, -18.6) * mm, "end": v(7.7, -18.57) * mm});
            skArc(sketch, "E11.20.12", {"start": v(8.05, -17.31) * mm, "mid": v(8.05, -17.27) * mm, "end": v(8.03, -17.22) * mm});
            skArc(sketch, "E11.20.13", {"start": v(6.5, -17.86) * mm, "mid": v(6.52, -17.9) * mm, "end": v(6.55, -17.94) * mm});
            skLineSegment(sketch, "E11.21.0", {"start": v(9.5, -16.46) * mm, "end": v(9, -15.57) * mm});
            skPoint(sketch, "E11.21.1", {"position": v(10.93, -15.6) * mm});
            skArc(sketch, "E11.21.2", {"start": v(9.56, -16.53) * mm, "mid": v(9.97, -16.82) * mm, "end": v(10.4, -17.06) * mm});
            skPoint(sketch, "E11.21.3", {"position": v(9.53, -16.5) * mm});
            skArc(sketch, "E11.21.4", {"start": v(10.94, -15.65) * mm, "mid": v(11.03, -16.14) * mm, "end": v(11.07, -16.64) * mm});
            skPoint(sketch, "E11.21.5", {"position": v(11.07, -16.78) * mm});
            skPoint(sketch, "E11.21.6", {"position": v(10.53, -17.12) * mm});
            skLineSegment(sketch, "E11.21.7", {"start": v(10.9, -15.57) * mm, "end": v(10.31, -14.73) * mm});
            skArc(sketch, "E11.21.8", {"start": v(10.95, -16.86) * mm, "mid": v(11.04, -16.77) * mm, "end": v(11.07, -16.64) * mm});
            skArc(sketch, "E11.21.9", {"start": v(10.95, -16.86) * mm, "mid": v(10.88, -16.9) * mm, "end": v(10.8, -16.96) * mm});
            skArc(sketch, "E11.21.10", {"start": v(10.4, -17.06) * mm, "mid": v(10.53, -17.09) * mm, "end": v(10.65, -17.05) * mm});
            skArc(sketch, "E11.21.11", {"start": v(10.65, -17.05) * mm, "mid": v(10.73, -17) * mm, "end": v(10.8, -16.96) * mm});
            skArc(sketch, "E11.21.12", {"start": v(10.94, -15.65) * mm, "mid": v(10.92, -15.6) * mm, "end": v(10.9, -15.57) * mm});
            skArc(sketch, "E11.21.13", {"start": v(9.5, -16.46) * mm, "mid": v(9.53, -16.5) * mm, "end": v(9.56, -16.53) * mm});
            skLineSegment(sketch, "E11.22.0", {"start": v(12.21, -14.56) * mm, "end": v(11.56, -13.78) * mm});
            skPoint(sketch, "E11.22.1", {"position": v(13.47, -13.47) * mm});
            skArc(sketch, "E11.22.2", {"start": v(12.29, -14.62) * mm, "mid": v(12.74, -14.83) * mm, "end": v(13.2, -15) * mm});
            skPoint(sketch, "E11.22.3", {"position": v(12.25, -14.6) * mm});
            skArc(sketch, "E11.22.4", {"start": v(13.5, -13.52) * mm, "mid": v(13.66, -13.98) * mm, "end": v(13.79, -14.47) * mm});
            skPoint(sketch, "E11.22.5", {"position": v(13.81, -14.6) * mm});
            skPoint(sketch, "E11.22.6", {"position": v(13.35, -15.03) * mm});
            skLineSegment(sketch, "E11.22.7", {"start": v(13.44, -13.44) * mm, "end": v(12.72, -12.72) * mm});
            skArc(sketch, "E11.22.8", {"start": v(13.71, -14.7) * mm, "mid": v(13.78, -14.6) * mm, "end": v(13.79, -14.47) * mm});
            skArc(sketch, "E11.22.9", {"start": v(13.71, -14.7) * mm, "mid": v(13.65, -14.76) * mm, "end": v(13.58, -14.82) * mm});
            skArc(sketch, "E11.22.10", {"start": v(13.2, -15) * mm, "mid": v(13.34, -15) * mm, "end": v(13.45, -14.94) * mm});
            skArc(sketch, "E11.22.11", {"start": v(13.45, -14.94) * mm, "mid": v(13.52, -14.88) * mm, "end": v(13.58, -14.82) * mm});
            skArc(sketch, "E11.22.12", {"start": v(13.5, -13.52) * mm, "mid": v(13.47, -13.47) * mm, "end": v(13.44, -13.44) * mm});
            skArc(sketch, "E11.22.13", {"start": v(12.21, -14.56) * mm, "mid": v(12.25, -14.6) * mm, "end": v(12.29, -14.62) * mm});
            skLineSegment(sketch, "E11.23.0", {"start": v(14.56, -12.21) * mm, "end": v(13.78, -11.56) * mm});
            skPoint(sketch, "E11.23.1", {"position": v(15.6, -10.93) * mm});
            skArc(sketch, "E11.23.2", {"start": v(14.64, -12.26) * mm, "mid": v(15.12, -12.4) * mm, "end": v(15.61, -12.47) * mm});
            skPoint(sketch, "E11.23.3", {"position": v(14.6, -12.25) * mm});
            skArc(sketch, "E11.23.4", {"start": v(15.63, -10.97) * mm, "mid": v(15.88, -11.4) * mm, "end": v(16.1, -11.85) * mm});
            skPoint(sketch, "E11.23.5", {"position": v(16.14, -11.99) * mm});
            skPoint(sketch, "E11.23.6", {"position": v(15.76, -12.49) * mm});
            skLineSegment(sketch, "E11.23.7", {"start": v(15.57, -10.9) * mm, "end": v(14.73, -10.31) * mm});
            skArc(sketch, "E11.23.8", {"start": v(16.06, -12.1) * mm, "mid": v(16.1, -11.98) * mm, "end": v(16.1, -11.85) * mm});
            skArc(sketch, "E11.23.9", {"start": v(16.06, -12.1) * mm, "mid": v(16, -12.17) * mm, "end": v(15.95, -12.24) * mm});
            skArc(sketch, "E11.23.10", {"start": v(15.61, -12.47) * mm, "mid": v(15.74, -12.46) * mm, "end": v(15.84, -12.38) * mm});
            skArc(sketch, "E11.23.11", {"start": v(15.84, -12.38) * mm, "mid": v(15.9, -12.3) * mm, "end": v(15.95, -12.24) * mm});
            skArc(sketch, "E11.23.12", {"start": v(15.63, -10.97) * mm, "mid": v(15.6, -10.93) * mm, "end": v(15.57, -10.9) * mm});
            skArc(sketch, "E11.23.13", {"start": v(14.56, -12.21) * mm, "mid": v(14.6, -12.24) * mm, "end": v(14.64, -12.26) * mm});
            skLineSegment(sketch, "E11.24.0", {"start": v(16.46, -9.5) * mm, "end": v(15.57, -9) * mm});
            skPoint(sketch, "E11.24.1", {"position": v(17.27, -8.05) * mm});
            skArc(sketch, "E11.24.2", {"start": v(16.55, -9.53) * mm, "mid": v(17.04, -9.58) * mm, "end": v(17.54, -9.57) * mm});
            skPoint(sketch, "E11.24.3", {"position": v(16.5, -9.53) * mm});
            skArc(sketch, "E11.24.4", {"start": v(17.3, -8.09) * mm, "mid": v(17.62, -8.47) * mm, "end": v(17.9, -8.88) * mm});
            skPoint(sketch, "E11.24.5", {"position": v(17.98, -9) * mm});
            skPoint(sketch, "E11.24.6", {"position": v(17.68, -9.56) * mm});
            skLineSegment(sketch, "E11.24.7", {"start": v(17.22, -8.03) * mm, "end": v(16.3, -7.6) * mm});
            skArc(sketch, "E11.24.8", {"start": v(17.91, -9.13) * mm, "mid": v(17.94, -9) * mm, "end": v(17.9, -8.88) * mm});
            skArc(sketch, "E11.24.9", {"start": v(17.91, -9.13) * mm, "mid": v(17.87, -9.2) * mm, "end": v(17.83, -9.28) * mm});
            skArc(sketch, "E11.24.10", {"start": v(17.54, -9.57) * mm, "mid": v(17.66, -9.53) * mm, "end": v(17.75, -9.44) * mm});
            skArc(sketch, "E11.24.11", {"start": v(17.75, -9.44) * mm, "mid": v(17.8, -9.36) * mm, "end": v(17.83, -9.28) * mm});
            skArc(sketch, "E11.24.12", {"start": v(17.3, -8.09) * mm, "mid": v(17.26, -8.05) * mm, "end": v(17.22, -8.03) * mm});
            skArc(sketch, "E11.24.13", {"start": v(16.46, -9.5) * mm, "mid": v(16.5, -9.52) * mm, "end": v(16.55, -9.53) * mm});
            skLineSegment(sketch, "E11.25.0", {"start": v(17.86, -6.5) * mm, "end": v(16.9, -6.15) * mm});
            skPoint(sketch, "E11.25.1", {"position": v(18.4, -4.93) * mm});
            skArc(sketch, "E11.25.2", {"start": v(17.95, -6.51) * mm, "mid": v(18.45, -6.47) * mm, "end": v(18.94, -6.38) * mm});
            skPoint(sketch, "E11.25.3", {"position": v(17.9, -6.52) * mm});
            skArc(sketch, "E11.25.4", {"start": v(18.44, -4.96) * mm, "mid": v(18.82, -5.28) * mm, "end": v(19.17, -5.63) * mm});
            skPoint(sketch, "E11.25.5", {"position": v(19.27, -5.74) * mm});
            skPoint(sketch, "E11.25.6", {"position": v(19.08, -6.35) * mm});
            skLineSegment(sketch, "E11.25.7", {"start": v(18.35, -4.92) * mm, "end": v(17.37, -4.65) * mm});
            skArc(sketch, "E11.25.8", {"start": v(19.23, -5.88) * mm, "mid": v(19.23, -5.75) * mm, "end": v(19.17, -5.63) * mm});
            skArc(sketch, "E11.25.9", {"start": v(19.23, -5.88) * mm, "mid": v(19.2, -5.96) * mm, "end": v(19.17, -6.05) * mm});
            skArc(sketch, "E11.25.10", {"start": v(18.94, -6.38) * mm, "mid": v(19.05, -6.32) * mm, "end": v(19.12, -6.21) * mm});
            skArc(sketch, "E11.25.11", {"start": v(19.12, -6.21) * mm, "mid": v(19.15, -6.13) * mm, "end": v(19.17, -6.05) * mm});
            skArc(sketch, "E11.25.12", {"start": v(18.44, -4.96) * mm, "mid": v(18.4, -4.93) * mm, "end": v(18.35, -4.92) * mm});
            skArc(sketch, "E11.25.13", {"start": v(17.86, -6.5) * mm, "mid": v(17.9, -6.51) * mm, "end": v(17.95, -6.51) * mm});
            skLineSegment(sketch, "E11.26.0", {"start": v(18.71, -3.3) * mm, "end": v(17.7, -3.12) * mm});
            skPoint(sketch, "E11.26.1", {"position": v(18.98, -1.66) * mm});
            skArc(sketch, "E11.26.2", {"start": v(18.8, -3.3) * mm, "mid": v(19.3, -3.17) * mm, "end": v(19.76, -3) * mm});
            skPoint(sketch, "E11.26.3", {"position": v(18.76, -3.3) * mm});
            skArc(sketch, "E11.26.4", {"start": v(19.02, -1.68) * mm, "mid": v(19.46, -1.93) * mm, "end": v(19.86, -2.22) * mm});
            skPoint(sketch, "E11.26.5", {"position": v(19.97, -2.31) * mm});
            skPoint(sketch, "E11.26.6", {"position": v(19.89, -2.94) * mm});
            skLineSegment(sketch, "E11.26.7", {"start": v(18.93, -1.66) * mm, "end": v(17.91, -1.57) * mm});
            skArc(sketch, "E11.26.8", {"start": v(19.95, -2.45) * mm, "mid": v(19.94, -2.32) * mm, "end": v(19.86, -2.22) * mm});
            skArc(sketch, "E11.26.9", {"start": v(19.95, -2.45) * mm, "mid": v(19.94, -2.54) * mm, "end": v(19.93, -2.62) * mm});
            skArc(sketch, "E11.26.10", {"start": v(19.76, -3) * mm, "mid": v(19.86, -2.92) * mm, "end": v(19.9, -2.8) * mm});
            skArc(sketch, "E11.26.11", {"start": v(19.9, -2.8) * mm, "mid": v(19.92, -2.71) * mm, "end": v(19.93, -2.62) * mm});
            skArc(sketch, "E11.26.12", {"start": v(19.02, -1.68) * mm, "mid": v(18.98, -1.66) * mm, "end": v(18.93, -1.66) * mm});
            skArc(sketch, "E11.26.13", {"start": v(18.71, -3.3) * mm, "mid": v(18.76, -3.3) * mm, "end": v(18.8, -3.3) * mm});
            skLineSegment(sketch, "E11.27.0", {"start": v(19, 0) * mm, "end": v(17.98, 0) * mm});
            skPoint(sketch, "E11.27.1", {"position": v(18.98, 1.66) * mm});
            skArc(sketch, "E11.27.2", {"start": v(19.1, 0.02) * mm, "mid": v(19.55, 0.23) * mm, "end": v(19.98, 0.48) * mm});
            skPoint(sketch, "E11.27.3", {"position": v(19.05, 0) * mm});
            skArc(sketch, "E11.27.4", {"start": v(19.02, 1.65) * mm, "mid": v(19.5, 1.48) * mm, "end": v(19.94, 1.26) * mm});
            skPoint(sketch, "E11.27.5", {"position": v(20.07, 1.2) * mm});
            skPoint(sketch, "E11.27.6", {"position": v(20.1, 0.56) * mm});
            skLineSegment(sketch, "E11.27.7", {"start": v(18.93, 1.66) * mm, "end": v(17.91, 1.57) * mm});
            skArc(sketch, "E11.27.8", {"start": v(20.08, 1.05) * mm, "mid": v(20.04, 1.18) * mm, "end": v(19.94, 1.26) * mm});
            skArc(sketch, "E11.27.9", {"start": v(20.08, 1.05) * mm, "mid": v(20.08, 0.97) * mm, "end": v(20.08, 0.88) * mm});
            skArc(sketch, "E11.27.10", {"start": v(19.98, 0.48) * mm, "mid": v(20.06, 0.58) * mm, "end": v(20.1, 0.7) * mm});
            skArc(sketch, "E11.27.11", {"start": v(20.1, 0.7) * mm, "mid": v(20.09, 0.79) * mm, "end": v(20.08, 0.88) * mm});
            skArc(sketch, "E11.27.12", {"start": v(19.02, 1.65) * mm, "mid": v(18.98, 1.66) * mm, "end": v(18.93, 1.66) * mm});
            skArc(sketch, "E11.27.13", {"start": v(19, 0) * mm, "mid": v(19.05, 0) * mm, "end": v(19.1, 0.02) * mm});
            skLineSegment(sketch, "E11.28.0", {"start": v(18.71, 3.3) * mm, "end": v(17.7, 3.12) * mm});
            skPoint(sketch, "E11.28.1", {"position": v(18.4, 4.93) * mm});
            skArc(sketch, "E11.28.2", {"start": v(18.8, 3.33) * mm, "mid": v(19.21, 3.62) * mm, "end": v(19.6, 3.94) * mm});
            skPoint(sketch, "E11.28.3", {"position": v(18.76, 3.3) * mm});
            skArc(sketch, "E11.28.4", {"start": v(18.45, 4.93) * mm, "mid": v(18.94, 4.84) * mm, "end": v(19.42, 4.7) * mm});
            skPoint(sketch, "E11.28.5", {"position": v(19.56, 4.66) * mm});
            skPoint(sketch, "E11.28.6", {"position": v(19.7, 4.04) * mm});
            skLineSegment(sketch, "E11.28.7", {"start": v(18.35, 4.92) * mm, "end": v(17.37, 4.65) * mm});
            skArc(sketch, "E11.28.8", {"start": v(19.59, 4.52) * mm, "mid": v(19.53, 4.64) * mm, "end": v(19.42, 4.7) * mm});
            skArc(sketch, "E11.28.9", {"start": v(19.59, 4.52) * mm, "mid": v(19.6, 4.44) * mm, "end": v(19.63, 4.35) * mm});
            skArc(sketch, "E11.28.10", {"start": v(19.6, 3.94) * mm, "mid": v(19.66, 4.05) * mm, "end": v(19.67, 4.18) * mm});
            skArc(sketch, "E11.28.11", {"start": v(19.67, 4.18) * mm, "mid": v(19.65, 4.27) * mm, "end": v(19.63, 4.35) * mm});
            skArc(sketch, "E11.28.12", {"start": v(18.45, 4.93) * mm, "mid": v(18.4, 4.93) * mm, "end": v(18.35, 4.92) * mm});
            skArc(sketch, "E11.28.13", {"start": v(18.71, 3.3) * mm, "mid": v(18.76, 3.31) * mm, "end": v(18.8, 3.33) * mm});
            skLineSegment(sketch, "E11.29.0", {"start": v(17.86, 6.5) * mm, "end": v(16.9, 6.15) * mm});
            skPoint(sketch, "E11.29.1", {"position": v(17.27, 8.05) * mm});
            skArc(sketch, "E11.29.2", {"start": v(17.94, 6.55) * mm, "mid": v(18.3, 6.9) * mm, "end": v(18.6, 7.28) * mm});
            skPoint(sketch, "E11.29.3", {"position": v(17.9, 6.52) * mm});
            skArc(sketch, "E11.29.4", {"start": v(17.31, 8.05) * mm, "mid": v(17.81, 8.06) * mm, "end": v(18.3, 8) * mm});
            skPoint(sketch, "E11.29.5", {"position": v(18.45, 7.98) * mm});
            skPoint(sketch, "E11.29.6", {"position": v(18.7, 7.4) * mm});
            skLineSegment(sketch, "E11.29.7", {"start": v(17.22, 8.03) * mm, "end": v(16.3, 7.6) * mm});
            skArc(sketch, "E11.29.8", {"start": v(18.5, 7.86) * mm, "mid": v(18.43, 7.96) * mm, "end": v(18.3, 8) * mm});
            skArc(sketch, "E11.29.9", {"start": v(18.5, 7.86) * mm, "mid": v(18.54, 7.78) * mm, "end": v(18.57, 7.7) * mm});
            skArc(sketch, "E11.29.10", {"start": v(18.6, 7.28) * mm, "mid": v(18.66, 7.4) * mm, "end": v(18.64, 7.53) * mm});
            skArc(sketch, "E11.29.11", {"start": v(18.64, 7.53) * mm, "mid": v(18.6, 7.61) * mm, "end": v(18.57, 7.7) * mm});
            skArc(sketch, "E11.29.12", {"start": v(17.31, 8.05) * mm, "mid": v(17.27, 8.05) * mm, "end": v(17.22, 8.03) * mm});
            skArc(sketch, "E11.29.13", {"start": v(17.86, 6.5) * mm, "mid": v(17.9, 6.52) * mm, "end": v(17.94, 6.55) * mm});
            skLineSegment(sketch, "E11.30.0", {"start": v(16.46, 9.5) * mm, "end": v(15.57, 9) * mm});
            skPoint(sketch, "E11.30.1", {"position": v(15.6, 10.93) * mm});
            skArc(sketch, "E11.30.2", {"start": v(16.53, 9.56) * mm, "mid": v(16.82, 9.97) * mm, "end": v(17.06, 10.4) * mm});
            skPoint(sketch, "E11.30.3", {"position": v(16.5, 9.52) * mm});
            skArc(sketch, "E11.30.4", {"start": v(15.65, 10.94) * mm, "mid": v(16.14, 11.03) * mm, "end": v(16.64, 11.07) * mm});
            skPoint(sketch, "E11.30.5", {"position": v(16.78, 11.07) * mm});
            skPoint(sketch, "E11.30.6", {"position": v(17.12, 10.53) * mm});
            skLineSegment(sketch, "E11.30.7", {"start": v(15.57, 10.9) * mm, "end": v(14.73, 10.31) * mm});
            skArc(sketch, "E11.30.8", {"start": v(16.86, 10.95) * mm, "mid": v(16.77, 11.04) * mm, "end": v(16.64, 11.07) * mm});
            skArc(sketch, "E11.30.9", {"start": v(16.86, 10.95) * mm, "mid": v(16.9, 10.88) * mm, "end": v(16.96, 10.8) * mm});
            skArc(sketch, "E11.30.10", {"start": v(17.06, 10.4) * mm, "mid": v(17.09, 10.53) * mm, "end": v(17.05, 10.65) * mm});
            skArc(sketch, "E11.30.11", {"start": v(17.05, 10.65) * mm, "mid": v(17, 10.73) * mm, "end": v(16.96, 10.8) * mm});
            skArc(sketch, "E11.30.12", {"start": v(15.65, 10.94) * mm, "mid": v(15.6, 10.92) * mm, "end": v(15.57, 10.9) * mm});
            skArc(sketch, "E11.30.13", {"start": v(16.46, 9.5) * mm, "mid": v(16.5, 9.53) * mm, "end": v(16.53, 9.56) * mm});
            skLineSegment(sketch, "E11.31.0", {"start": v(14.56, 12.21) * mm, "end": v(13.78, 11.56) * mm});
            skPoint(sketch, "E11.31.1", {"position": v(13.47, 13.47) * mm});
            skArc(sketch, "E11.31.2", {"start": v(14.62, 12.29) * mm, "mid": v(14.83, 12.74) * mm, "end": v(15, 13.2) * mm});
            skPoint(sketch, "E11.31.3", {"position": v(14.6, 12.25) * mm});
            skArc(sketch, "E11.31.4", {"start": v(13.52, 13.5) * mm, "mid": v(13.98, 13.66) * mm, "end": v(14.47, 13.79) * mm});
            skPoint(sketch, "E11.31.5", {"position": v(14.6, 13.81) * mm});
            skPoint(sketch, "E11.31.6", {"position": v(15.03, 13.35) * mm});
            skLineSegment(sketch, "E11.31.7", {"start": v(13.44, 13.44) * mm, "end": v(12.72, 12.72) * mm});
            skArc(sketch, "E11.31.8", {"start": v(14.7, 13.71) * mm, "mid": v(14.6, 13.78) * mm, "end": v(14.47, 13.79) * mm});
            skArc(sketch, "E11.31.9", {"start": v(14.7, 13.71) * mm, "mid": v(14.76, 13.65) * mm, "end": v(14.82, 13.58) * mm});
            skArc(sketch, "E11.31.10", {"start": v(15, 13.2) * mm, "mid": v(15, 13.34) * mm, "end": v(14.94, 13.45) * mm});
            skArc(sketch, "E11.31.11", {"start": v(14.94, 13.45) * mm, "mid": v(14.88, 13.52) * mm, "end": v(14.82, 13.58) * mm});
            skArc(sketch, "E11.31.12", {"start": v(13.52, 13.5) * mm, "mid": v(13.47, 13.47) * mm, "end": v(13.44, 13.44) * mm});
            skArc(sketch, "E11.31.13", {"start": v(14.56, 12.21) * mm, "mid": v(14.6, 12.25) * mm, "end": v(14.62, 12.29) * mm});
            skLineSegment(sketch, "E11.32.0", {"start": v(12.21, 14.56) * mm, "end": v(11.56, 13.78) * mm});
            skPoint(sketch, "E11.32.1", {"position": v(10.93, 15.6) * mm});
            skArc(sketch, "E11.32.2", {"start": v(12.26, 14.64) * mm, "mid": v(12.4, 15.12) * mm, "end": v(12.47, 15.61) * mm});
            skPoint(sketch, "E11.32.3", {"position": v(12.25, 14.6) * mm});
            skArc(sketch, "E11.32.4", {"start": v(10.97, 15.63) * mm, "mid": v(11.4, 15.88) * mm, "end": v(11.85, 16.1) * mm});
            skPoint(sketch, "E11.32.5", {"position": v(11.99, 16.14) * mm});
            skPoint(sketch, "E11.32.6", {"position": v(12.49, 15.76) * mm});
            skLineSegment(sketch, "E11.32.7", {"start": v(10.9, 15.57) * mm, "end": v(10.31, 14.73) * mm});
            skArc(sketch, "E11.32.8", {"start": v(12.1, 16.06) * mm, "mid": v(11.98, 16.1) * mm, "end": v(11.85, 16.1) * mm});
            skArc(sketch, "E11.32.9", {"start": v(12.1, 16.06) * mm, "mid": v(12.17, 16) * mm, "end": v(12.24, 15.95) * mm});
            skArc(sketch, "E11.32.10", {"start": v(12.47, 15.61) * mm, "mid": v(12.46, 15.74) * mm, "end": v(12.38, 15.84) * mm});
            skArc(sketch, "E11.32.11", {"start": v(12.38, 15.84) * mm, "mid": v(12.3, 15.9) * mm, "end": v(12.24, 15.95) * mm});
            skArc(sketch, "E11.32.12", {"start": v(10.97, 15.63) * mm, "mid": v(10.93, 15.6) * mm, "end": v(10.9, 15.57) * mm});
            skArc(sketch, "E11.32.13", {"start": v(12.21, 14.56) * mm, "mid": v(12.24, 14.6) * mm, "end": v(12.26, 14.64) * mm});
            skLineSegment(sketch, "E11.33.0", {"start": v(9.5, 16.46) * mm, "end": v(9, 15.57) * mm});
            skPoint(sketch, "E11.33.1", {"position": v(8.05, 17.27) * mm});
            skArc(sketch, "E11.33.2", {"start": v(9.53, 16.55) * mm, "mid": v(9.58, 17.04) * mm, "end": v(9.57, 17.54) * mm});
            skPoint(sketch, "E11.33.3", {"position": v(9.52, 16.5) * mm});
            skArc(sketch, "E11.33.4", {"start": v(8.09, 17.3) * mm, "mid": v(8.47, 17.62) * mm, "end": v(8.88, 17.9) * mm});
            skPoint(sketch, "E11.33.5", {"position": v(9, 17.98) * mm});
            skPoint(sketch, "E11.33.6", {"position": v(9.56, 17.68) * mm});
            skLineSegment(sketch, "E11.33.7", {"start": v(8.03, 17.22) * mm, "end": v(7.6, 16.3) * mm});
            skArc(sketch, "E11.33.8", {"start": v(9.13, 17.91) * mm, "mid": v(9, 17.94) * mm, "end": v(8.88, 17.9) * mm});
            skArc(sketch, "E11.33.9", {"start": v(9.13, 17.91) * mm, "mid": v(9.2, 17.87) * mm, "end": v(9.28, 17.83) * mm});
            skArc(sketch, "E11.33.10", {"start": v(9.57, 17.54) * mm, "mid": v(9.53, 17.66) * mm, "end": v(9.44, 17.75) * mm});
            skArc(sketch, "E11.33.11", {"start": v(9.44, 17.75) * mm, "mid": v(9.36, 17.8) * mm, "end": v(9.28, 17.83) * mm});
            skArc(sketch, "E11.33.12", {"start": v(8.09, 17.3) * mm, "mid": v(8.05, 17.26) * mm, "end": v(8.03, 17.22) * mm});
            skArc(sketch, "E11.33.13", {"start": v(9.5, 16.46) * mm, "mid": v(9.52, 16.5) * mm, "end": v(9.53, 16.55) * mm});
            skLineSegment(sketch, "E11.34.0", {"start": v(6.5, 17.86) * mm, "end": v(6.15, 16.9) * mm});
            skPoint(sketch, "E11.34.1", {"position": v(4.93, 18.4) * mm});
            skArc(sketch, "E11.34.2", {"start": v(6.51, 17.95) * mm, "mid": v(6.47, 18.45) * mm, "end": v(6.38, 18.94) * mm});
            skPoint(sketch, "E11.34.3", {"position": v(6.52, 17.9) * mm});
            skArc(sketch, "E11.34.4", {"start": v(4.96, 18.44) * mm, "mid": v(5.28, 18.82) * mm, "end": v(5.63, 19.17) * mm});
            skPoint(sketch, "E11.34.5", {"position": v(5.74, 19.27) * mm});
            skPoint(sketch, "E11.34.6", {"position": v(6.35, 19.08) * mm});
            skLineSegment(sketch, "E11.34.7", {"start": v(4.92, 18.35) * mm, "end": v(4.65, 17.37) * mm});
            skArc(sketch, "E11.34.8", {"start": v(5.88, 19.23) * mm, "mid": v(5.75, 19.23) * mm, "end": v(5.63, 19.17) * mm});
            skArc(sketch, "E11.34.9", {"start": v(5.88, 19.23) * mm, "mid": v(5.96, 19.2) * mm, "end": v(6.05, 19.17) * mm});
            skArc(sketch, "E11.34.10", {"start": v(6.38, 18.94) * mm, "mid": v(6.32, 19.05) * mm, "end": v(6.21, 19.12) * mm});
            skArc(sketch, "E11.34.11", {"start": v(6.21, 19.12) * mm, "mid": v(6.13, 19.15) * mm, "end": v(6.05, 19.17) * mm});
            skArc(sketch, "E11.34.12", {"start": v(4.96, 18.44) * mm, "mid": v(4.93, 18.4) * mm, "end": v(4.92, 18.35) * mm});
            skArc(sketch, "E11.34.13", {"start": v(6.5, 17.86) * mm, "mid": v(6.51, 17.9) * mm, "end": v(6.51, 17.95) * mm});
            skLineSegment(sketch, "E11.35.0", {"start": v(3.3, 18.71) * mm, "end": v(3.12, 17.7) * mm});
            skPoint(sketch, "E11.35.1", {"position": v(1.66, 18.98) * mm});
            skArc(sketch, "E11.35.2", {"start": v(3.3, 18.8) * mm, "mid": v(3.17, 19.3) * mm, "end": v(3, 19.76) * mm});
            skPoint(sketch, "E11.35.3", {"position": v(3.3, 18.76) * mm});
            skArc(sketch, "E11.35.4", {"start": v(1.68, 19.02) * mm, "mid": v(1.93, 19.46) * mm, "end": v(2.22, 19.86) * mm});
            skPoint(sketch, "E11.35.5", {"position": v(2.31, 19.97) * mm});
            skPoint(sketch, "E11.35.6", {"position": v(2.94, 19.89) * mm});
            skLineSegment(sketch, "E11.35.7", {"start": v(1.66, 18.93) * mm, "end": v(1.57, 17.91) * mm});
            skArc(sketch, "E11.35.8", {"start": v(2.45, 19.95) * mm, "mid": v(2.32, 19.94) * mm, "end": v(2.22, 19.86) * mm});
            skArc(sketch, "E11.35.9", {"start": v(2.45, 19.95) * mm, "mid": v(2.54, 19.94) * mm, "end": v(2.62, 19.93) * mm});
            skArc(sketch, "E11.35.10", {"start": v(3, 19.76) * mm, "mid": v(2.92, 19.86) * mm, "end": v(2.8, 19.9) * mm});
            skArc(sketch, "E11.35.11", {"start": v(2.8, 19.9) * mm, "mid": v(2.71, 19.92) * mm, "end": v(2.62, 19.93) * mm});
            skArc(sketch, "E11.35.12", {"start": v(1.68, 19.02) * mm, "mid": v(1.66, 18.98) * mm, "end": v(1.66, 18.93) * mm});
            skArc(sketch, "E11.35.13", {"start": v(3.3, 18.71) * mm, "mid": v(3.3, 18.76) * mm, "end": v(3.3, 18.8) * mm});
            skSolve(sketch);
        }
        {
            var Q0;
            Q0 = qSketchRegion(id + "F0", true);
            var Q1;
            {var subQ0=sQuery(id+"F0.wireOp",EDGE,"E0");var subQ35=makeQuery(id+"F0.imprint","INTERSECT",VERTEX,{"derivedFrom":[subQ0,sQuery(id+"F0.wireOp",EDGE,"E11.27.0")]});Q1=makeQuery(id+"F0.imprint","IMPRINT",FACE,{"disambiguationData":[TD([[makeQuery(id+"F0.imprint","IMPRINT",EDGE,{"disambiguationData":[TD([[subQ35,-1.0]])],"derivedFrom":subQ0}),1.0]])]});}
            extrude(context, id + "F1", {"entities" : qUnion([Q0, Q1]), "depth" : 6.35 * mm});
        }
        {
            var Q0;
            Q0=qCreatedBy(makeId("Front.planeOp"),FACE);
            var sketch = newSketch(context, id + "F2", { "sketchPlane" : qUnion([Q0])});
            skCircle(sketch, "E12", {"center": v(0, 0) * mm, "radius": 5.59 * mm});
            skSolve(sketch);
        }
        {
            var Q0;
            Q0=makeQuery(id+"F2.imprint","IMPRINT",FACE,{"disambiguationData":[TD([[makeQuery(id+"F2.imprint","IMPRINT",EDGE,{"derivedFrom":sQuery(id+"F2.wireOp",EDGE,"E12")}),1.0]])]});
            extrude(context, id + "F3", {"entities" : qUnion([Q0]), "operationType" : NewBodyOperationType.REMOVE, "depth" : 12.7 * mm});
        }
    });
